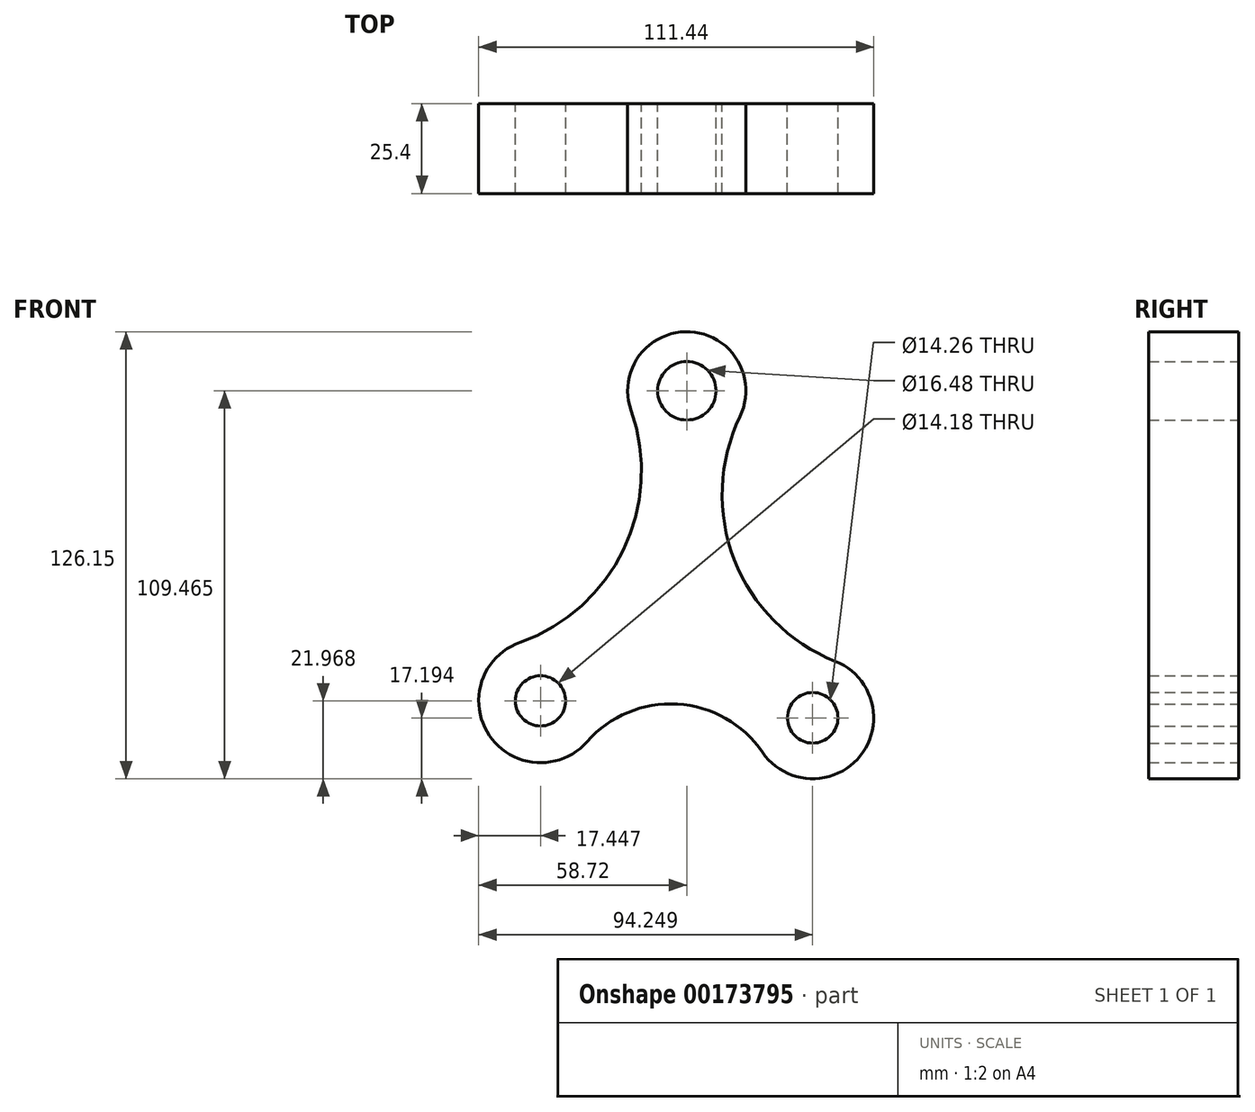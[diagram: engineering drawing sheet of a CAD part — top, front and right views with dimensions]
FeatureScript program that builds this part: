
annotation { "Feature Type Name" : "Feature", "Feature Type Description" : "" }
export const myFeature = defineFeature(function(context is Context, id is Id, definition is map)
    precondition{}
    {
        {
            var Q0;
            Q0=qCreatedBy(makeId("Front.planeOp"),FACE);
            var sketch = newSketch(context, id + "F0", { "sketchPlane" : qUnion([Q0])});
            skCircle(sketch, "E0", {"center": v(0, 51.69) * mm, "radius": 16.68 * mm});
            skCircle(sketch, "E1", {"center": v(-41.27, -35.81) * mm, "radius": 17.45 * mm});
            skCircle(sketch, "E2", {"center": v(35.53, -40.59) * mm, "radius": 17.2 * mm});
            skPoint(sketch, "E3.first.point", {"position": v(-43.22, -18.47) * mm});
            skPoint(sketch, "E3.second.point", {"position": v(-13.97, 42.58) * mm});
            skPoint(sketch, "E3.third.point", {"position": v(-99.88, 60.35) * mm});
            skArc(sketch, "E4", {"start": v(21.36, -50.32) * mm, "mid": v(-2.68, -36.73) * mm, "end": v(-28.18, -47.34) * mm});
            skArc(sketch, "E5", {"start": v(-47.09, -19.36) * mm, "mid": v(-17.86, 6.9) * mm, "end": v(-15.74, 46.15) * mm});
            skArc(sketch, "E6", {"start": v(15.02, 44.42) * mm, "mid": v(13.41, 4.06) * mm, "end": v(41.88, -24.6) * mm});
            skCircle(sketch, "E7", {"center": v(0, 51.69) * mm, "radius": 8.24 * mm});
            skCircle(sketch, "E8", {"center": v(-41.27, -35.81) * mm, "radius": 7.1 * mm});
            skCircle(sketch, "E9", {"center": v(35.53, -40.59) * mm, "radius": 7.13 * mm});
            skSolve(sketch);
        }
        {
            var Q0;
            {var subQ0=sQuery(id+"F0.wireOp",EDGE,"E4");Q0=makeQuery(id+"F0.imprint","IMPRINT",FACE,{"disambiguationData":[TD([[makeQuery(id+"F0.imprint","IMPRINT",EDGE,{"derivedFrom":subQ0}),-1.0]])]});}
            var Q1;
            Q1=makeQuery(id+"F0.imprint","IMPRINT",FACE,{"disambiguationData":[TD([[makeQuery(id+"F0.imprint","IMPRINT",EDGE,{"derivedFrom":sQuery(id+"F0.wireOp",EDGE,"E7")}),-1.0]])]});
            var Q2;
            Q2=makeQuery(id+"F0.imprint","IMPRINT",FACE,{"disambiguationData":[TD([[makeQuery(id+"F0.imprint","IMPRINT",EDGE,{"derivedFrom":sQuery(id+"F0.wireOp",EDGE,"E8")}),-1.0]])]});
            var Q3;
            Q3=makeQuery(id+"F0.imprint","IMPRINT",FACE,{"disambiguationData":[TD([[makeQuery(id+"F0.imprint","IMPRINT",EDGE,{"derivedFrom":sQuery(id+"F0.wireOp",EDGE,"E9")}),-1.0]])]});
            extrude(context, id + "F1", {"entities" : qUnion([Q0, Q1, Q2, Q3]), "depth" : 25.4 * mm});
        }
    });
